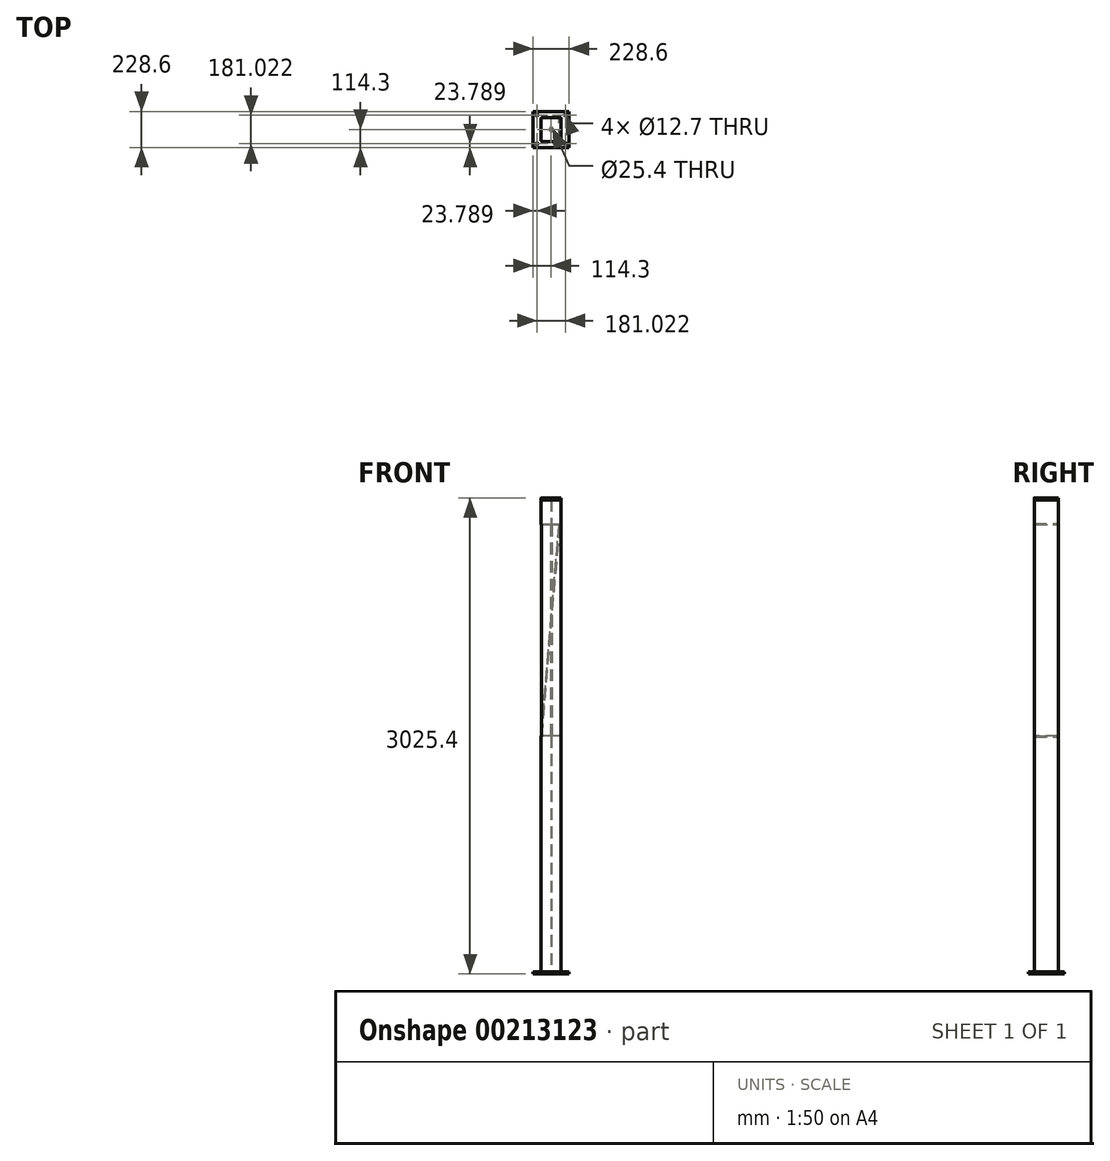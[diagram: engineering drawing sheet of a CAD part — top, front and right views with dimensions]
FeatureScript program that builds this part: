
annotation { "Feature Type Name" : "Feature", "Feature Type Description" : "" }
export const myFeature = defineFeature(function(context is Context, id is Id, definition is map)
    precondition{}
    {
        {
            var Q0;
            Q0=qCreatedBy(makeId("Top.planeOp"),FACE);
            var sketch = newSketch(context, id + "F0", { "sketchPlane" : qUnion([Q0])});
            skLineSegment(sketch, "E0", {"start": v(63.62, -69.64) * mm, "end": v(63.62, 71.65) * mm});
            skLineSegment(sketch, "E1", {"start": v(58.86, 76.41) * mm, "end": v(8.37, 76.41) * mm});
            skLineSegment(sketch, "E2", {"start": v(0.12, 68.16) * mm, "end": v(0.12, 59.83) * mm});
            skLineSegment(sketch, "E3", {"start": v(63.62, 0.21) * mm, "end": v(1.03, 0.21) * mm, "construction": true});
            skPoint(sketch, "E3.endSnap0", {"position": v(63.62, 0.21) * mm});
            skLineSegment(sketch, "E4.MirrorCS", {"start": v(57.27, -75.99) * mm, "end": v(8.37, -75.99) * mm});
            skLineSegment(sketch, "E5.MirrorCS", {"start": v(0.12, -67.74) * mm, "end": v(0.12, -59.4) * mm});
            skLineSegment(sketch, "E6.2", {"start": v(55.37, -74.09) * mm, "end": v(8.37, -74.09) * mm});
            skLineSegment(sketch, "E6.3", {"start": v(61.72, -67.74) * mm, "end": v(61.72, 69.75) * mm});
            skLineSegment(sketch, "E6.4", {"start": v(56.96, 74.51) * mm, "end": v(8.37, 74.51) * mm});
            skLineSegment(sketch, "E7.MirrorCS", {"start": v(0.12, 68.16) * mm, "end": v(0.12, 56.11) * mm});
            skPoint(sketch, "E8.visualSharp", {"position": v(61.72, 74.51) * mm});
            skArc(sketch, "E8.filletArc", {"start": v(61.72, 69.75) * mm, "mid": v(60.33, 73.12) * mm, "end": v(56.96, 74.51) * mm});
            skPoint(sketch, "E9.visualSharp", {"position": v(63.62, 76.41) * mm});
            skArc(sketch, "E9.filletArc", {"start": v(63.62, 71.65) * mm, "mid": v(62.23, 75.02) * mm, "end": v(58.86, 76.41) * mm});
            skPoint(sketch, "E10.visualSharp", {"position": v(61.72, -74.09) * mm});
            skArc(sketch, "E10.filletArc", {"start": v(55.37, -74.09) * mm, "mid": v(59.86, -72.23) * mm, "end": v(61.72, -67.74) * mm});
            skPoint(sketch, "E11.visualSharp", {"position": v(63.62, -75.99) * mm});
            skArc(sketch, "E11.filletArc", {"start": v(57.27, -75.99) * mm, "mid": v(61.76, -74.13) * mm, "end": v(63.62, -69.64) * mm});
            skPoint(sketch, "E12.visualSharp", {"position": v(2.02, -74.09) * mm});
            skArc(sketch, "E13.0", {"start": v(3.1, -74.09) * mm, "mid": v(5.57, -75.5) * mm, "end": v(8.37, -75.99) * mm});
            skPoint(sketch, "E14.orphan", {"position": v(0.12, -75.99) * mm});
            skArc(sketch, "E15.MirrorCS", {"start": v(3.1, 74.51) * mm, "mid": v(5.57, 75.92) * mm, "end": v(8.37, 76.41) * mm});
            skPoint(sketch, "E16.orphan", {"position": v(0.12, 76.41) * mm});
            skLineSegment(sketch, "E17", {"start": v(0.12, 59.83) * mm, "end": v(0.12, -59.4) * mm, "construction": true});
            skArc(sketch, "E18.MirrorCS", {"start": v(-2.86, 74.51) * mm, "mid": v(-5.33, 75.92) * mm, "end": v(-8.13, 76.41) * mm});
            skLineSegment(sketch, "E19.MirrorCS", {"start": v(-56.72, 74.51) * mm, "end": v(-8.13, 74.51) * mm});
            skLineSegment(sketch, "E20.MirrorCS", {"start": v(-58.62, 76.41) * mm, "end": v(-8.13, 76.41) * mm});
            skArc(sketch, "E21.MirrorCS", {"start": v(-61.48, 69.75) * mm, "mid": v(-60.08, 73.12) * mm, "end": v(-56.72, 74.51) * mm});
            skPoint(sketch, "E22.MirrorP", {"position": v(-61.48, 74.51) * mm});
            skArc(sketch, "E23.MirrorCS", {"start": v(-63.38, 71.65) * mm, "mid": v(-61.98, 75.02) * mm, "end": v(-58.62, 76.41) * mm});
            skLineSegment(sketch, "E24.MirrorCS", {"start": v(-63.38, -69.64) * mm, "end": v(-63.38, 71.65) * mm});
            skLineSegment(sketch, "E25.MirrorCS", {"start": v(-61.48, -67.74) * mm, "end": v(-61.48, 69.75) * mm});
            skArc(sketch, "E26.MirrorCS", {"start": v(-57.03, -75.99) * mm, "mid": v(-61.52, -74.13) * mm, "end": v(-63.38, -69.64) * mm});
            skArc(sketch, "E27.MirrorCS", {"start": v(-55.13, -74.09) * mm, "mid": v(-59.62, -72.23) * mm, "end": v(-61.48, -67.74) * mm});
            skLineSegment(sketch, "E28.MirrorCS", {"start": v(-55.13, -74.09) * mm, "end": v(-8.13, -74.09) * mm});
            skLineSegment(sketch, "E29.MirrorCS", {"start": v(-57.03, -75.99) * mm, "end": v(-8.13, -75.99) * mm});
            skArc(sketch, "E30.MirrorCS", {"start": v(-2.86, -74.09) * mm, "mid": v(-5.33, -75.5) * mm, "end": v(-8.13, -75.99) * mm});
            skLineSegment(sketch, "E31", {"start": v(-8.13, 74.51) * mm, "end": v(8.37, 74.51) * mm});
            skLineSegment(sketch, "E32", {"start": v(-1.8, 68.16) * mm, "end": v(-1.78, 68.16) * mm});
            skLineSegment(sketch, "E33.bottom", {"start": v(61.1, 35.3) * mm, "end": v(-28.9, 35.3) * mm, "construction": true});
            skLineSegment(sketch, "E33.top", {"start": v(61.1, -54.7) * mm, "end": v(-28.9, -54.7) * mm, "construction": true});
            skLineSegment(sketch, "E33.left", {"start": v(61.1, 35.3) * mm, "end": v(61.1, -54.7) * mm, "construction": true});
            skLineSegment(sketch, "E33.right", {"start": v(-28.9, 35.3) * mm, "end": v(-28.9, -54.7) * mm, "construction": true});
            skPoint(sketch, "E33.middle", {"position": v(0, -9.7) * mm});
            skPoint(sketch, "E34.orphan", {"position": v(-1.78, 68.16) * mm});
            skPoint(sketch, "E35.MirrorCS.end.orphan", {"position": v(-1.78, 40) * mm});
            skPoint(sketch, "E35.MirrorCS.start.orphan", {"position": v(0.12, 59.83) * mm});
            skLineSegment(sketch, "E36", {"start": v(18.98, 50.3) * mm, "end": v(122.62, -251.36) * mm, "construction": true});
            skLineSegment(sketch, "E37", {"start": v(51.6, 74.51) * mm, "end": v(-61.48, 35.67) * mm, "construction": true});
            skPoint(sketch, "E38.orphan", {"position": v(43.27, 71.65) * mm});
            skPoint(sketch, "E39.orphan", {"position": v(0.12, 68.16) * mm});
            skPoint(sketch, "E40.MirrorCS.start.orphan", {"position": v(2.02, 68.16) * mm});
            skPoint(sketch, "E41.MirrorCS.end.orphan", {"position": v(-8.13, -74.09) * mm});
            skPoint(sketch, "E41.MirrorCS.start.orphan", {"position": v(-1.78, -67.74) * mm});
            skPoint(sketch, "E42.orphan", {"position": v(0.12, -67.74) * mm});
            skPoint(sketch, "E6.1.start.orphan", {"position": v(2.02, -67.74) * mm});
            skPoint(sketch, "E43.MirrorCS.end.orphan", {"position": v(-1.78, -59.4) * mm});
            skPoint(sketch, "E44.MirrorCS.end.orphan", {"position": v(0.12, -59.4) * mm});
            skPoint(sketch, "E45.end.orphan", {"position": v(2.02, -59.4) * mm});
            skLineSegment(sketch, "E46", {"start": v(-8.13, -74.09) * mm, "end": v(-2.86, -74.09) * mm});
            skLineSegment(sketch, "E47", {"start": v(3.1, -74.09) * mm, "end": v(8.37, -74.09) * mm});
            skLineSegment(sketch, "E48", {"start": v(-2.86, -74.09) * mm, "end": v(3.1, -74.09) * mm});
            skLineSegment(sketch, "E49", {"start": v(8.37, -75.99) * mm, "end": v(-8.13, -75.99) * mm});
            skLineSegment(sketch, "E50", {"start": v(-8.13, 76.41) * mm, "end": v(8.37, 76.41) * mm});
            skSolve(sketch);
        }
        {
            var Q0;
            {var subQ1=sQuery(id+"F0.wireOp",EDGE,"E18.MirrorCS");Q0=makeQuery(id+"F0.imprint","IMPRINT",FACE,{"disambiguationData":[TD([[makeQuery(id+"F0.imprint","IMPRINT",EDGE,{"derivedFrom":subQ1}),1.0]])]});}
            var Q1;
            {var subQ0=sQuery(id+"F0.wireOp",EDGE,"E15.MirrorCS");Q1=makeQuery(id+"F0.imprint","IMPRINT",FACE,{"disambiguationData":[TD([[makeQuery(id+"F0.imprint","IMPRINT",EDGE,{"derivedFrom":subQ0}),1.0]])]});}
            var Q2;
            Q2=makeQuery(id+"F0.imprint","IMPRINT",FACE,{"disambiguationData":[TD([[makeQuery(id+"F0.imprint","IMPRINT",EDGE,{"derivedFrom":sQuery(id+"F0.wireOp",EDGE,"E0")}),1.0]])]});
            var Q3;
            Q3=makeQuery(id+"F0.imprint","IMPRINT",FACE,{"disambiguationData":[TD([[makeQuery(id+"F0.imprint","IMPRINT",EDGE,{"derivedFrom":sQuery(id+"F0.wireOp",EDGE,"E13.0")}),-1.0]])]});
            extrude(context, id + "F1", {"entities" : qUnion([Q0, Q1, Q2, Q3]), "endBound" : BoundingType.SYMMETRIC, "depth" : 3000 * mm});
        }
        {
            var Q0;
            Q0=makeQuery(id+"F1.opExtrude","CAP_FACE",FACE,{"disambiguationData":[OSD([sQuery(id+"F0.wireOp",EDGE,"E0"),sQuery(id+"F0.wireOp",EDGE,"E1"),sQuery(id+"F0.wireOp",EDGE,"E4.MirrorCS"),sQuery(id+"F0.wireOp",EDGE,"E6.0"),sQuery(id+"F0.wireOp",EDGE,"E6.1"),sQuery(id+"F0.wireOp",EDGE,"E6.2"),sQuery(id+"F0.wireOp",EDGE,"E6.3"),sQuery(id+"F0.wireOp",EDGE,"E6.4"),sQuery(id+"F0.wireOp",EDGE,"E45"),sQuery(id+"F0.wireOp",EDGE,"BmveN9TY-At4n-m40N-BZ4B-1K53SQ1AOBh2"),sQuery(id+"F0.wireOp",EDGE,"E8.filletArc"),sQuery(id+"F0.wireOp",EDGE,"E9.filletArc"),sQuery(id+"F0.wireOp",EDGE,"E10.filletArc"),sQuery(id+"F0.wireOp",EDGE,"E11.filletArc"),sQuery(id+"F0.wireOp",EDGE,"E12.filletArc"),sQuery(id+"F0.wireOp",EDGE,"E13.0"),sQuery(id+"F0.wireOp",EDGE,"E15.MirrorCS"),sQuery(id+"F0.wireOp",EDGE,"E40.MirrorCS"),sQuery(id+"F0.wireOp",EDGE,"c3247eec-0fe1-41a2-8665-72d71258245c0.MirrorCS"),sQuery(id+"F0.wireOp",EDGE,"E18.MirrorCS"),sQuery(id+"F0.wireOp",EDGE,"5c1b336e-1487-4cab-a79d-06dbedb42d290.MirrorCS"),sQuery(id+"F0.wireOp",EDGE,"E19.MirrorCS"),sQuery(id+"F0.wireOp",EDGE,"E20.MirrorCS"),sQuery(id+"F0.wireOp",EDGE,"E21.MirrorCS"),sQuery(id+"F0.wireOp",EDGE,"E23.MirrorCS"),sQuery(id+"F0.wireOp",EDGE,"E24.MirrorCS"),sQuery(id+"F0.wireOp",EDGE,"E25.MirrorCS"),sQuery(id+"F0.wireOp",EDGE,"E26.MirrorCS"),sQuery(id+"F0.wireOp",EDGE,"E27.MirrorCS"),sQuery(id+"F0.wireOp",EDGE,"E28.MirrorCS"),sQuery(id+"F0.wireOp",EDGE,"E29.MirrorCS"),sQuery(id+"F0.wireOp",EDGE,"E30.MirrorCS"),sQuery(id+"F0.wireOp",EDGE,"E41.MirrorCS"),sQuery(id+"F0.wireOp",EDGE,"E43.MirrorCS"),sQuery(id+"F0.wireOp",EDGE,"ce2e3958-069b-4034-b1eb-0fb900c1421d0.MirrorCS"),sQuery(id+"F0.wireOp",EDGE,"E35.MirrorCS")])],"isStart":false});
            var sketch = newSketch(context, id + "F2", { "sketchPlane" : qUnion([Q0])});
            skLineSegment(sketch, "E51.bottom", {"start": v(-57.03, 76.41) * mm, "end": v(57.18, 76.41) * mm});
            skLineSegment(sketch, "E51.top", {"start": v(-57.03, -75.82) * mm, "end": v(57.18, -75.82) * mm});
            skLineSegment(sketch, "E51.left", {"start": v(-63.38, 70.06) * mm, "end": v(-63.38, -69.47) * mm});
            skLineSegment(sketch, "E51.right", {"start": v(63.53, 70.06) * mm, "end": v(63.53, -69.47) * mm});
            skPoint(sketch, "E52.visualSharp", {"position": v(-63.38, 76.41) * mm});
            skArc(sketch, "E52.filletArc", {"start": v(-57.03, 76.41) * mm, "mid": v(-61.52, 74.55) * mm, "end": v(-63.38, 70.06) * mm});
            skPoint(sketch, "E53.visualSharp", {"position": v(63.53, 76.41) * mm});
            skArc(sketch, "E53.filletArc", {"start": v(63.53, 70.06) * mm, "mid": v(61.67, 74.55) * mm, "end": v(57.18, 76.41) * mm});
            skPoint(sketch, "E54.visualSharp", {"position": v(63.53, -75.82) * mm});
            skArc(sketch, "E54.filletArc", {"start": v(57.18, -75.82) * mm, "mid": v(61.67, -73.96) * mm, "end": v(63.53, -69.47) * mm});
            skPoint(sketch, "E55.visualSharp", {"position": v(-63.38, -75.82) * mm});
            skArc(sketch, "E55.filletArc", {"start": v(-63.38, -69.47) * mm, "mid": v(-61.52, -73.96) * mm, "end": v(-57.03, -75.82) * mm});
            skSolve(sketch);
        }
        {
            var Q0;
            Q0 = qSketchRegion(id + "F2", true);
            extrude(context, id + "F3", {"entities" : qUnion([Q0]), "operationType" : NewBodyOperationType.ADD, "depth" : 12.7 * mm});
        }
        {
            var Q0;
            Q0=makeQuery(id+"F1.opExtrude","CAP_FACE",FACE,{"disambiguationData":[OSD([sQuery(id+"F0.wireOp",EDGE,"E0"),sQuery(id+"F0.wireOp",EDGE,"E1"),sQuery(id+"F0.wireOp",EDGE,"E4.MirrorCS"),sQuery(id+"F0.wireOp",EDGE,"E6.0"),sQuery(id+"F0.wireOp",EDGE,"E6.1"),sQuery(id+"F0.wireOp",EDGE,"E6.2"),sQuery(id+"F0.wireOp",EDGE,"E6.3"),sQuery(id+"F0.wireOp",EDGE,"E6.4"),sQuery(id+"F0.wireOp",EDGE,"E45"),sQuery(id+"F0.wireOp",EDGE,"BmveN9TY-At4n-m40N-BZ4B-1K53SQ1AOBh2"),sQuery(id+"F0.wireOp",EDGE,"E8.filletArc"),sQuery(id+"F0.wireOp",EDGE,"E9.filletArc"),sQuery(id+"F0.wireOp",EDGE,"E10.filletArc"),sQuery(id+"F0.wireOp",EDGE,"E11.filletArc"),sQuery(id+"F0.wireOp",EDGE,"E12.filletArc"),sQuery(id+"F0.wireOp",EDGE,"E13.0"),sQuery(id+"F0.wireOp",EDGE,"E15.MirrorCS"),sQuery(id+"F0.wireOp",EDGE,"E40.MirrorCS"),sQuery(id+"F0.wireOp",EDGE,"c3247eec-0fe1-41a2-8665-72d71258245c0.MirrorCS"),sQuery(id+"F0.wireOp",EDGE,"E18.MirrorCS"),sQuery(id+"F0.wireOp",EDGE,"5c1b336e-1487-4cab-a79d-06dbedb42d290.MirrorCS"),sQuery(id+"F0.wireOp",EDGE,"E19.MirrorCS"),sQuery(id+"F0.wireOp",EDGE,"E20.MirrorCS"),sQuery(id+"F0.wireOp",EDGE,"E21.MirrorCS"),sQuery(id+"F0.wireOp",EDGE,"E23.MirrorCS"),sQuery(id+"F0.wireOp",EDGE,"E24.MirrorCS"),sQuery(id+"F0.wireOp",EDGE,"E25.MirrorCS"),sQuery(id+"F0.wireOp",EDGE,"E26.MirrorCS"),sQuery(id+"F0.wireOp",EDGE,"E27.MirrorCS"),sQuery(id+"F0.wireOp",EDGE,"E28.MirrorCS"),sQuery(id+"F0.wireOp",EDGE,"E29.MirrorCS"),sQuery(id+"F0.wireOp",EDGE,"E30.MirrorCS"),sQuery(id+"F0.wireOp",EDGE,"E41.MirrorCS"),sQuery(id+"F0.wireOp",EDGE,"E43.MirrorCS"),sQuery(id+"F0.wireOp",EDGE,"ce2e3958-069b-4034-b1eb-0fb900c1421d0.MirrorCS"),sQuery(id+"F0.wireOp",EDGE,"E35.MirrorCS")])],"isStart":true});
            var sketch = newSketch(context, id + "F4", { "sketchPlane" : qUnion([Q0])});
            skCircle(sketch, "E56", {"center": v(90.51, -90.51) * mm, "radius": 6.35 * mm});
            skCircle(sketch, "E57.MirrorC", {"center": v(90.51, 90.51) * mm, "radius": 6.35 * mm});
            skCircle(sketch, "E58.MirrorC", {"center": v(-90.51, 90.51) * mm, "radius": 6.35 * mm});
            skCircle(sketch, "E59.MirrorC", {"center": v(-90.51, -90.51) * mm, "radius": 6.35 * mm});
            skLineSegment(sketch, "E60.bottom", {"start": v(-114.3, 114.3) * mm, "end": v(114.3, 114.3) * mm});
            skLineSegment(sketch, "E60.top", {"start": v(-114.3, -114.3) * mm, "end": v(114.3, -114.3) * mm});
            skLineSegment(sketch, "E60.left", {"start": v(-114.3, 114.3) * mm, "end": v(-114.3, -114.3) * mm});
            skLineSegment(sketch, "E60.right", {"start": v(114.3, 114.3) * mm, "end": v(114.3, -114.3) * mm});
            skPoint(sketch, "E60.middle", {"position": v(0, 0) * mm});
            skLineSegment(sketch, "E61.top", {"start": v(-90.51, -90.51) * mm, "end": v(90.51, -90.51) * mm, "construction": true});
            skLineSegment(sketch, "E61.left", {"start": v(-90.51, 90.51) * mm, "end": v(-90.51, -90.51) * mm, "construction": true});
            skLineSegment(sketch, "E62.bottom", {"start": v(63.62, 78.78) * mm, "end": v(-63.62, 78.78) * mm, "construction": true});
            skLineSegment(sketch, "E62.top", {"start": v(63.62, -78.78) * mm, "end": v(-63.62, -78.78) * mm, "construction": true});
            skLineSegment(sketch, "E62.left", {"start": v(63.62, 78.78) * mm, "end": v(63.62, -78.78) * mm, "construction": true});
            skLineSegment(sketch, "E62.right", {"start": v(-63.62, 78.78) * mm, "end": v(-63.62, -78.78) * mm, "construction": true});
            skLineSegment(sketch, "E63", {"start": v(-90.51, 90.51) * mm, "end": v(90.51, 90.51) * mm, "construction": true});
            skLineSegment(sketch, "E64", {"start": v(90.51, -90.51) * mm, "end": v(90.51, 90.51) * mm, "construction": true});
            skCircle(sketch, "E65", {"center": v(0, 0) * mm, "radius": 12.7 * mm});
            skSolve(sketch);
        }
        {
            var Q0;
            Q0 = qSketchRegion(id + "F4", true);
            extrude(context, id + "F5", {"entities" : qUnion([Q0]), "depth" : 12.7 * mm});
        }
        {
            var Q0;
            Q0=qCreatedBy(makeId("Front.planeOp"),FACE);
            var sketch = newSketch(context, id + "F6", { "sketchPlane" : qUnion([Q0])});
            skLineSegment(sketch, "E66", {"start": v(-60.14, 0) * mm, "end": v(52.93, 1344.56) * mm, "construction": true});
            skLineSegment(sketch, "E67", {"start": v(52.93, 1344.56) * mm, "end": v(52.93, 1514.56) * mm, "construction": true});
            skLineSegment(sketch, "E68.0", {"start": v(-58.2, -5.16) * mm, "end": v(55.3, 1344.48) * mm});
            skLineSegment(sketch, "E69.0", {"start": v(-62.78, -3.26) * mm, "end": v(50.92, 1348.84) * mm});
            skLineSegment(sketch, "E70", {"start": v(-62.78, -3.26) * mm, "end": v(-58.2, -5.16) * mm});
            skLineSegment(sketch, "E71", {"start": v(50.92, 1348.84) * mm, "end": v(55.3, 1344.48) * mm});
            skSolve(sketch);
        }
        {
            var Q0;
            Q0 = qSketchRegion(id + "F6", true);
            extrude(context, id + "F7", {"entities" : qUnion([Q0]), "operationType" : NewBodyOperationType.ADD, "endBound" : BoundingType.SYMMETRIC, "depth" : 144 * mm});
        }
        {
            var Q0;
            Q0=makeQuery(id+"F3.boolean.opBoolean","MERGE",FACE,{"derivedFrom":[makeQuery(id+"F1.opExtrude","SWEPT_FACE",FACE,{"disambiguationData":[OSD([sQuery(id+"F0.wireOp",EDGE,"E24.MirrorCS")])]}),makeQuery(id+"F3.opExtrude","SWEPT_FACE",FACE,{"disambiguationData":[OSD([sQuery(id+"F2.wireOp",EDGE,"E51.left")])]})]});
            var sketch = newSketch(context, id + "F8", { "sketchPlane" : qUnion([Q0])});
            skLineSegment(sketch, "E72", {"start": v(-0.3, 1512.7) * mm, "end": v(-0.3, 1342.7) * mm, "construction": true});
            skPoint(sketch, "E73.startSnap0", {"position": v(-71.65, 0) * mm});
            skLineSegment(sketch, "E74", {"start": v(-0.3, 1342.7) * mm, "end": v(-75.1, 1342.7) * mm});
            skLineSegment(sketch, "E75", {"start": v(-75.1, 1342.7) * mm, "end": v(-75.1, 0) * mm});
            skLineSegment(sketch, "E76", {"start": v(-75.1, 0) * mm, "end": v(0, 0) * mm});
            skLineSegment(sketch, "E77.MirrorCS", {"start": v(-0.3, 1342.7) * mm, "end": v(74.51, 1342.7) * mm});
            skLineSegment(sketch, "E78.MirrorCS", {"start": v(74.51, 1342.7) * mm, "end": v(74.51, 0) * mm});
            skLineSegment(sketch, "E79.MirrorCS", {"start": v(74.51, 0) * mm, "end": v(-0.6, 0) * mm});
            skSolve(sketch);
        }
        {
            var Q0;
            Q0 = qSketchRegion(id + "F8", true);
            extrude(context, id + "F9", {"entities" : qUnion([Q0]), "operationType" : NewBodyOperationType.REMOVE, "oppositeDirection" : true, "depth" : 123 * mm});
        }
        {
            var Q0;
            Q0 = qSketchRegion(id + "F6", true);
            extrude(context, id + "F10", {"entities" : qUnion([Q0]), "operationType" : NewBodyOperationType.ADD, "endBound" : BoundingType.SYMMETRIC, "depth" : 152.4 * mm - 1.9 * mm - 1.9 * mm});
        }
        {
            var Q0;
            {var subQ0=sQuery(id+"F6.wireOp",EDGE,"E69.0");Q0=makeQuery(id+"F10.boolean.opBoolean","MERGE",FACE,{"derivedFrom":[makeQuery(id+"F7.opExtrude","SWEPT_FACE",FACE,{"disambiguationData":[OSD([subQ0])]}),makeQuery(id+"F10.opExtrude","SWEPT_FACE",FACE,{"disambiguationData":[OSD([subQ0])]})]});}
            var sketch = newSketch(context, id + "F11", { "sketchPlane" : qUnion([Q0])});
            skLineSegment(sketch, "E80", {"start": v(0, 1348.36) * mm, "end": v(-0.1, 1166.51) * mm, "construction": true});
            skPoint(sketch, "E80.endSnap0", {"position": v(-0.1, 1348.36) * mm});
            skArc(sketch, "E81", {"start": v(-41, 1348.36) * mm, "mid": v(-23.38, 1331.07) * mm, "end": v(-0.01, 1323.1) * mm});
            skArc(sketch, "E82.MirrorCS", {"start": v(41, 1348.31) * mm, "mid": v(23.36, 1331.05) * mm, "end": v(-0.01, 1323.1) * mm});
            skLineSegment(sketch, "E83", {"start": v(-41, 1348.36) * mm, "end": v(41, 1348.31) * mm});
            skSolve(sketch);
        }
        {
            var Q0;
            Q0 = qSketchRegion(id + "F11", true);
            extrude(context, id + "F12", {"entities" : qUnion([Q0]), "operationType" : NewBodyOperationType.REMOVE, "depth" : 3 * mm});
        }
    });
